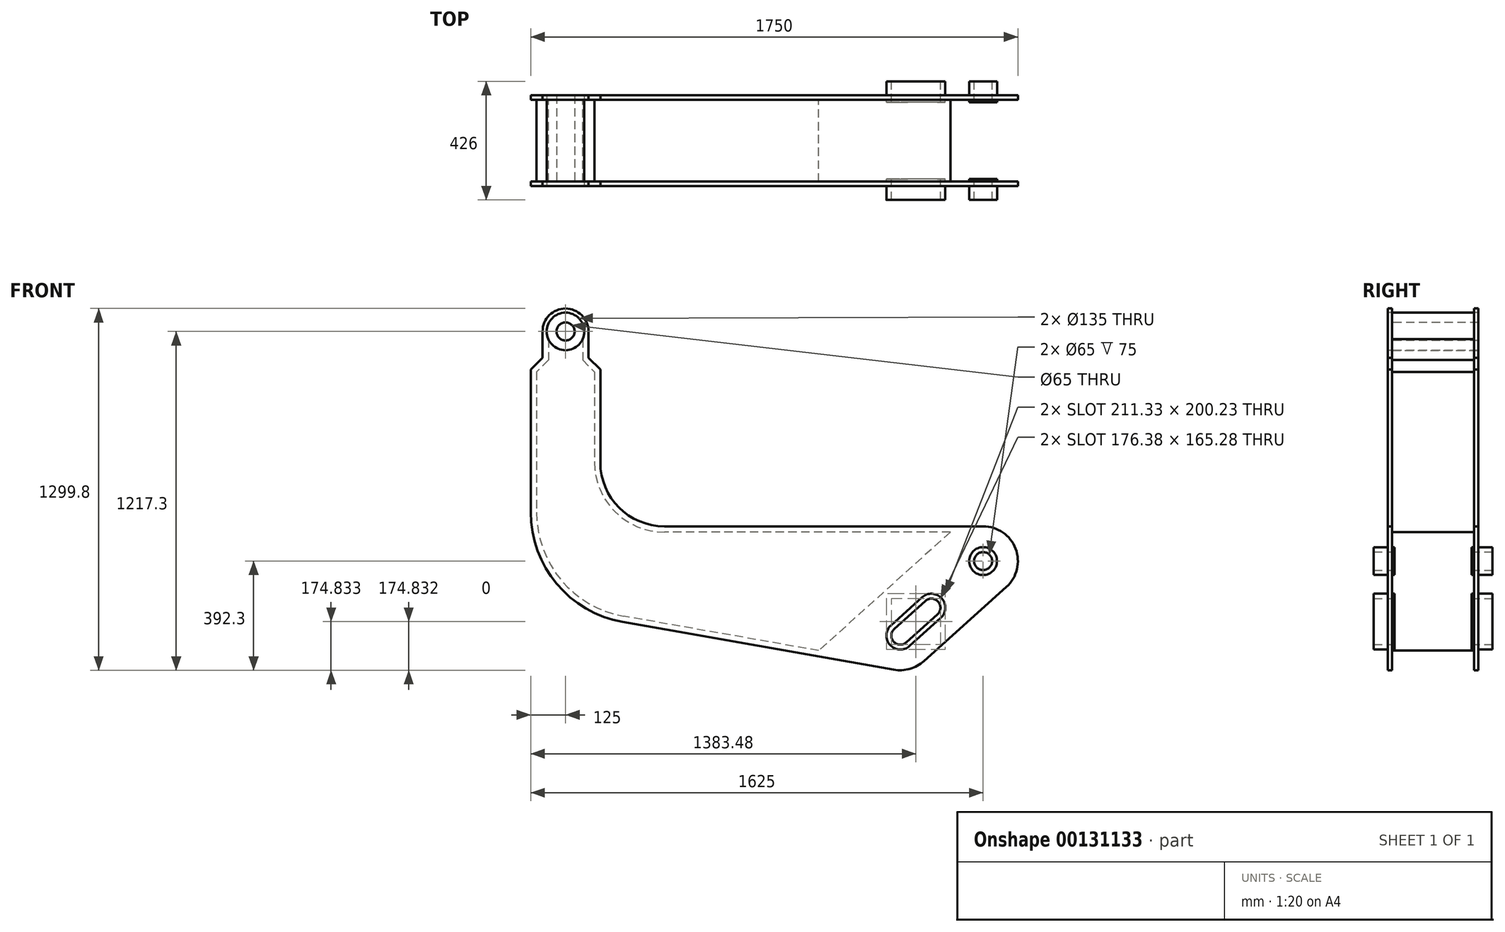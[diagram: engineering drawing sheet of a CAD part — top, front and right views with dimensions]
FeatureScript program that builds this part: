
annotation { "Feature Type Name" : "Feature", "Feature Type Description" : "" }
export const myFeature = defineFeature(function(context is Context, id is Id, definition is map)
    precondition{}
    {
        {
            var Q0;
            Q0=qCreatedBy(makeId("Front.planeOp"),FACE);
            var sketch = newSketch(context, id + "F0", { "sketchPlane" : qUnion([Q0])});
            skCircle(sketch, "E0", {"center": v(0, 0) * mm, "radius": 32.5 * mm});
            skCircle(sketch, "E1.0", {"center": v(0, 0) * mm, "radius": 82.5 * mm});
            skLineSegment(sketch, "E2", {"start": v(-82.5, 0) * mm, "end": v(-82.5, -94.13) * mm});
            skLineSegment(sketch, "E3", {"start": v(82.5, 0) * mm, "end": v(82.5, -94.13) * mm});
            skLineSegment(sketch, "E4", {"start": v(-82.5, -94.13) * mm, "end": v(-125, -136.63) * mm});
            skLineSegment(sketch, "E5", {"start": v(82.5, -94.13) * mm, "end": v(125, -136.63) * mm});
            skCircle(sketch, "E6", {"center": v(1500, -825) * mm, "radius": 32.5 * mm});
            skArc(sketch, "E7", {"start": v(1583.64, -917.9) * mm, "mid": v(1616.7, -780.2) * mm, "end": v(1500, -700) * mm});
            skCircle(sketch, "E8", {"center": v(1500, -825) * mm, "radius": 100 * mm});
            skLineSegment(sketch, "E9", {"start": v(1500, -825) * mm, "end": v(997.38, -825) * mm, "construction": true});
            skLineSegment(sketch, "E10", {"start": v(1500, -825) * mm, "end": v(1202.74, -1092.65) * mm, "construction": true});
            skLineSegment(sketch, "E11", {"start": v(1583.64, -917.9) * mm, "end": v(1288.2, -1183.91) * mm});
            skLineSegment(sketch, "E12", {"start": v(1178.63, -1215.33) * mm, "end": v(205.54, -1043.75) * mm});
            skLineSegment(sketch, "E13", {"start": v(1241.08, -1226.34) * mm, "end": v(892.28, -1226.34) * mm, "construction": true});
            skLineSegment(sketch, "E14", {"start": v(-125, -136.63) * mm, "end": v(-125, -649.82) * mm});
            skPoint(sketch, "E15.visualSharp", {"position": v(1241.08, -1226.34) * mm});
            skArc(sketch, "E15.filletArc", {"start": v(1178.63, -1215.33) * mm, "mid": v(1237.04, -1212.27) * mm, "end": v(1288.2, -1183.91) * mm});
            skPoint(sketch, "E16.visualSharp", {"position": v(-125, -985.46) * mm});
            skArc(sketch, "E16.filletArc", {"start": v(-125, -649.82) * mm, "mid": v(-31.42, -906.94) * mm, "end": v(205.54, -1043.75) * mm});
            skLineSegment(sketch, "E17", {"start": v(125, -136.63) * mm, "end": v(125, -470) * mm});
            skLineSegment(sketch, "E18", {"start": v(1500, -700) * mm, "end": v(355, -700) * mm});
            skPoint(sketch, "E19.visualSharp", {"position": v(125, -700) * mm});
            skArc(sketch, "E19.filletArc", {"start": v(125, -470) * mm, "mid": v(192.37, -632.63) * mm, "end": v(355, -700) * mm});
            skCircle(sketch, "E20", {"center": v(0, 0) * mm, "radius": 50 * mm});
            skCircle(sketch, "E21", {"center": v(1500, -825) * mm, "radius": 50 * mm});
            skCircle(sketch, "E22.0", {"center": v(0, 0) * mm, "radius": 67.5 * mm});
            skArc(sketch, "E23", {"start": v(1335.96, -1016.43) * mm, "mid": v(1338.37, -970.54) * mm, "end": v(1292.47, -968.13) * mm});
            skLineSegment(sketch, "E24", {"start": v(1335.96, -1016.43) * mm, "end": v(1224.49, -1116.8) * mm});
            skArc(sketch, "E25", {"start": v(1224.49, -1116.8) * mm, "mid": v(1178.59, -1114.4) * mm, "end": v(1181, -1068.5) * mm});
            skLineSegment(sketch, "E26", {"start": v(1292.47, -968.13) * mm, "end": v(1181, -1068.5) * mm});
            skLineSegment(sketch, "E27.0", {"start": v(1280.76, -955.13) * mm, "end": v(1169.29, -1055.5) * mm});
            skArc(sketch, "E27.1", {"start": v(1347.67, -1029.44) * mm, "mid": v(1351.37, -958.83) * mm, "end": v(1280.76, -955.13) * mm});
            skLineSegment(sketch, "E27.2", {"start": v(1347.67, -1029.44) * mm, "end": v(1236.2, -1129.8) * mm});
            skArc(sketch, "E27.3", {"start": v(1236.2, -1129.8) * mm, "mid": v(1165.58, -1126.1) * mm, "end": v(1169.29, -1055.5) * mm});
            skLineSegment(sketch, "E28.0", {"start": v(1247.3, -917.97) * mm, "end": v(1135.83, -1018.34) * mm});
            skArc(sketch, "E28.1", {"start": v(1381.13, -1066.6) * mm, "mid": v(1388.53, -925.37) * mm, "end": v(1247.3, -917.97) * mm});
            skLineSegment(sketch, "E28.2", {"start": v(1381.13, -1066.6) * mm, "end": v(1269.66, -1166.97) * mm});
            skArc(sketch, "E28.3", {"start": v(1269.66, -1166.97) * mm, "mid": v(1128.43, -1159.57) * mm, "end": v(1135.83, -1018.34) * mm});
            skSolve(sketch);
        }
        {
            var Q0;
            Q0 = qSketchRegion(id + "F0", true);
            var Q1;
            Q1=makeQuery(id+"F0.imprint","IMPRINT",FACE,{"disambiguationData":[TD([[makeQuery(id+"F0.imprint","IMPRINT",EDGE,{"derivedFrom":sQuery(id+"F0.wireOp",EDGE,"E8")}),1.0]])]});
            var Q2;
            Q2=makeQuery(id+"F0.imprint","IMPRINT",FACE,{"disambiguationData":[TD([[makeQuery(id+"F0.imprint","IMPRINT",EDGE,{"derivedFrom":sQuery(id+"F0.wireOp",EDGE,"VV7gzSqa-Ojlq-ZYf3-16EK-QqAcn2rNi812")}),1.0]])]});
            var Q3;
            Q3=makeQuery(id+"F0.imprint","IMPRINT",FACE,{"disambiguationData":[TD([[makeQuery(id+"F0.imprint","IMPRINT",EDGE,{"derivedFrom":sQuery(id+"F0.wireOp",EDGE,"E27.0")}),-1.0]])]});
            extrude(context, id + "F1", {"entities" : qUnion([Q0, Q1, Q2, Q3]), "depth" : 16 * mm});
        }
        {
            var Q0;
            Q0=makeQuery(id+"F1.opExtrude","CAP_FACE",FACE,{"disambiguationData":[OSD([sQuery(id+"F0.wireOp",EDGE,"E1.0"),sQuery(id+"F0.wireOp",EDGE,"E2"),sQuery(id+"F0.wireOp",EDGE,"E3"),sQuery(id+"F0.wireOp",EDGE,"E4"),sQuery(id+"F0.wireOp",EDGE,"E5"),sQuery(id+"F0.wireOp",EDGE,"E7"),sQuery(id+"F0.wireOp",EDGE,"E11"),sQuery(id+"F0.wireOp",EDGE,"E12"),sQuery(id+"F0.wireOp",EDGE,"E14"),sQuery(id+"F0.wireOp",EDGE,"E15.filletArc"),sQuery(id+"F0.wireOp",EDGE,"E16.filletArc"),sQuery(id+"F0.wireOp",EDGE,"E17"),sQuery(id+"F0.wireOp",EDGE,"E18"),sQuery(id+"F0.wireOp",EDGE,"E19.filletArc"),sQuery(id+"F0.wireOp",EDGE,"E21"),sQuery(id+"F0.wireOp",EDGE,"E22.0"),sQuery(id+"F0.wireOp",EDGE,"E27.0"),sQuery(id+"F0.wireOp",EDGE,"E27.1"),sQuery(id+"F0.wireOp",EDGE,"E27.2"),sQuery(id+"F0.wireOp",EDGE,"E27.3")])],"isStart":false});
            cPlane(context, id + "F2", {"entities" : qUnion([Q0]), "cplaneType" : CPlaneType.OFFSET, "offset" : 310 * mm, "width" : 150 * mm, "height" : 150 * mm});
        }
        {
            var Q0;
            Q0=qCreatedBy(id+"F2.planeOp",FACE);
            var sketch = newSketch(context, id + "F3", { "sketchPlane" : qUnion([Q0])});
            skCircle(sketch, "E29.0", {"center": v(0, 0) * mm, "radius": 32.5 * mm});
            skCircle(sketch, "E29.1", {"center": v(0, 0) * mm, "radius": 82.5 * mm});
            skLineSegment(sketch, "E29.2", {"start": v(-82.5, 0) * mm, "end": v(-82.5, -94.13) * mm});
            skLineSegment(sketch, "E29.3", {"start": v(82.5, 0) * mm, "end": v(82.5, -94.13) * mm});
            skLineSegment(sketch, "E29.4", {"start": v(-82.5, -94.13) * mm, "end": v(-125, -136.63) * mm});
            skLineSegment(sketch, "E29.5", {"start": v(82.5, -94.13) * mm, "end": v(125, -136.63) * mm});
            skCircle(sketch, "E29.6", {"center": v(1500, -825) * mm, "radius": 32.5 * mm});
            skArc(sketch, "E29.7", {"start": v(1583.64, -917.9) * mm, "mid": v(1616.7, -780.2) * mm, "end": v(1500, -700) * mm});
            skCircle(sketch, "E29.8", {"center": v(1500, -825) * mm, "radius": 100 * mm});
            skLineSegment(sketch, "E29.9", {"start": v(1500, -825) * mm, "end": v(997.38, -825) * mm});
            skLineSegment(sketch, "E29.10", {"start": v(1500, -825) * mm, "end": v(1202.74, -1092.65) * mm});
            skLineSegment(sketch, "E29.11", {"start": v(1583.64, -917.9) * mm, "end": v(1288.2, -1183.91) * mm});
            skLineSegment(sketch, "E29.12", {"start": v(1178.63, -1215.33) * mm, "end": v(205.54, -1043.75) * mm});
            skLineSegment(sketch, "E29.13", {"start": v(1241.08, -1226.34) * mm, "end": v(892.28, -1226.34) * mm});
            skLineSegment(sketch, "E29.14", {"start": v(-125, -136.63) * mm, "end": v(-125, -649.82) * mm});
            skPoint(sketch, "E29.15", {"position": v(1241.08, -1226.34) * mm});
            skArc(sketch, "E29.16", {"start": v(1178.63, -1215.33) * mm, "mid": v(1237.04, -1212.27) * mm, "end": v(1288.2, -1183.91) * mm});
            skPoint(sketch, "E29.17", {"position": v(-125, -985.46) * mm});
            skArc(sketch, "E29.18", {"start": v(-125, -649.82) * mm, "mid": v(-31.42, -906.94) * mm, "end": v(205.54, -1043.75) * mm});
            skLineSegment(sketch, "E29.19", {"start": v(125, -136.63) * mm, "end": v(125, -470) * mm});
            skLineSegment(sketch, "E29.20", {"start": v(1500, -700) * mm, "end": v(355, -700) * mm});
            skPoint(sketch, "E29.21", {"position": v(125, -700) * mm});
            skArc(sketch, "E29.22", {"start": v(125, -470) * mm, "mid": v(192.37, -632.63) * mm, "end": v(355, -700) * mm});
            skCircle(sketch, "E29.23", {"center": v(0, 0) * mm, "radius": 50 * mm});
            skCircle(sketch, "E29.24", {"center": v(1500, -825) * mm, "radius": 50 * mm});
            skCircle(sketch, "E29.25", {"center": v(0, 0) * mm, "radius": 67.5 * mm});
            skArc(sketch, "E29.26", {"start": v(1335.96, -1016.43) * mm, "mid": v(1338.37, -970.54) * mm, "end": v(1292.47, -968.13) * mm});
            skLineSegment(sketch, "E29.27", {"start": v(1335.96, -1016.43) * mm, "end": v(1224.49, -1116.8) * mm});
            skArc(sketch, "E29.28", {"start": v(1224.49, -1116.8) * mm, "mid": v(1178.59, -1114.4) * mm, "end": v(1181, -1068.5) * mm});
            skLineSegment(sketch, "E29.29", {"start": v(1292.47, -968.13) * mm, "end": v(1181, -1068.5) * mm});
            skLineSegment(sketch, "E29.30", {"start": v(1280.76, -955.13) * mm, "end": v(1169.29, -1055.5) * mm});
            skArc(sketch, "E29.31", {"start": v(1347.67, -1029.44) * mm, "mid": v(1351.37, -958.83) * mm, "end": v(1280.76, -955.13) * mm});
            skLineSegment(sketch, "E29.32", {"start": v(1347.67, -1029.44) * mm, "end": v(1236.2, -1129.8) * mm});
            skArc(sketch, "E29.33", {"start": v(1236.2, -1129.8) * mm, "mid": v(1165.58, -1126.1) * mm, "end": v(1169.29, -1055.5) * mm});
            skLineSegment(sketch, "E29.34", {"start": v(1247.3, -917.97) * mm, "end": v(1135.83, -1018.34) * mm});
            skArc(sketch, "E29.35", {"start": v(1381.13, -1066.6) * mm, "mid": v(1388.53, -925.37) * mm, "end": v(1247.3, -917.97) * mm});
            skLineSegment(sketch, "E29.36", {"start": v(1381.13, -1066.6) * mm, "end": v(1269.66, -1166.97) * mm});
            skArc(sketch, "E29.37", {"start": v(1269.66, -1166.97) * mm, "mid": v(1128.43, -1159.57) * mm, "end": v(1135.83, -1018.34) * mm});
            skSolve(sketch);
        }
        {
            var Q0;
            Q0 = qSketchRegion(id + "F3", true);
            var Q1;
            {var subQ0=sQuery(id+"F3.wireOp",EDGE,"E29.9");var subQ1=sQuery(id+"F3.wireOp",EDGE,"E29.8");var subQ2=makeQuery(id+"F3.imprint","INTERSECT",VERTEX,{"derivedFrom":[subQ1,subQ0]});Q1=makeQuery(id+"F3.imprint","IMPRINT",FACE,{"disambiguationData":[TD([[makeQuery(id+"F3.imprint","IMPRINT",EDGE,{"disambiguationData":[TD([[subQ2,1.0]])],"derivedFrom":subQ1}),1.0]])]});}
            var Q2;
            {var subQ0=sQuery(id+"F3.wireOp",EDGE,"E29.9");var subQ1=sQuery(id+"F3.wireOp",EDGE,"E29.8");var subQ2=makeQuery(id+"F3.imprint","INTERSECT",VERTEX,{"derivedFrom":[subQ1,subQ0]});Q2=makeQuery(id+"F3.imprint","IMPRINT",FACE,{"disambiguationData":[TD([[makeQuery(id+"F3.imprint","IMPRINT",EDGE,{"disambiguationData":[TD([[subQ2,-1.0]])],"derivedFrom":subQ1}),1.0]])]});}
            var Q3;
            {var subQ0=sQuery(id+"F3.wireOp",EDGE,"E29.9");var subQ1=sQuery(id+"F3.wireOp",EDGE,"E29.8");var subQ2=makeQuery(id+"F3.imprint","INTERSECT",VERTEX,{"derivedFrom":[subQ1,subQ0]});Q3=makeQuery(id+"F3.imprint","IMPRINT",FACE,{"disambiguationData":[TD([[makeQuery(id+"F3.imprint","IMPRINT",EDGE,{"disambiguationData":[TD([[subQ2,1.0]])],"derivedFrom":subQ1}),-1.0]])]});}
            var Q4;
            {var subQ0=sQuery(id+"F3.wireOp",EDGE,"E29.9");var subQ1=sQuery(id+"F3.wireOp",EDGE,"E29.8");var subQ2=makeQuery(id+"F3.imprint","INTERSECT",VERTEX,{"derivedFrom":[subQ1,subQ0]});Q4=makeQuery(id+"F3.imprint","IMPRINT",FACE,{"disambiguationData":[TD([[makeQuery(id+"F3.imprint","IMPRINT",EDGE,{"disambiguationData":[TD([[subQ2,-1.0]])],"derivedFrom":subQ1}),-1.0]])]});}
            var Q5;
            {var subQ2=sQuery(id+"F3.wireOp",EDGE,"E29.30");Q5=makeQuery(id+"F3.imprint","IMPRINT",FACE,{"disambiguationData":[TD([[makeQuery(id+"F3.imprint","IMPRINT",EDGE,{"derivedFrom":subQ2}),-1.0]])]});}
            extrude(context, id + "F4", {"entities" : qUnion([Q0, Q1, Q2, Q3, Q4, Q5]), "oppositeDirection" : true, "depth" : 16 * mm});
        }
        {
            var Q0;
            Q0=makeQuery(id+"F1.opExtrude","CAP_FACE",FACE,{"disambiguationData":[OSD([sQuery(id+"F0.wireOp",EDGE,"E0"),sQuery(id+"F0.wireOp",EDGE,"E1.0"),sQuery(id+"F0.wireOp",EDGE,"E2"),sQuery(id+"F0.wireOp",EDGE,"E3"),sQuery(id+"F0.wireOp",EDGE,"E4"),sQuery(id+"F0.wireOp",EDGE,"E5"),sQuery(id+"F0.wireOp",EDGE,"E7"),sQuery(id+"F0.wireOp",EDGE,"E11"),sQuery(id+"F0.wireOp",EDGE,"E12"),sQuery(id+"F0.wireOp",EDGE,"E14"),sQuery(id+"F0.wireOp",EDGE,"E15.filletArc"),sQuery(id+"F0.wireOp",EDGE,"E16.filletArc"),sQuery(id+"F0.wireOp",EDGE,"E17"),sQuery(id+"F0.wireOp",EDGE,"E18"),sQuery(id+"F0.wireOp",EDGE,"E19.filletArc"),sQuery(id+"F0.wireOp",EDGE,"E21"),sQuery(id+"F0.wireOp",EDGE,"NVSJcbsx-t4oL-S8TC-E93Z-FQbPMW0S7kzD")])],"isStart":false});
            var sketch = newSketch(context, id + "F5", { "sketchPlane" : qUnion([Q0])});
            skLineSegment(sketch, "E30.0", {"start": v(125, -136.63) * mm, "end": v(125, -470) * mm});
            skLineSegment(sketch, "E30.3", {"start": v(-125, -136.63) * mm, "end": v(-125, -649.82) * mm});
            skArc(sketch, "E30.4", {"start": v(125, -470) * mm, "mid": v(192.37, -632.63) * mm, "end": v(355, -700) * mm});
            skLineSegment(sketch, "E30.5", {"start": v(1500, -700) * mm, "end": v(355, -700) * mm});
            skArc(sketch, "E30.6", {"start": v(-125, -649.82) * mm, "mid": v(-31.42, -906.94) * mm, "end": v(205.54, -1043.75) * mm});
            skLineSegment(sketch, "E30.7", {"start": v(1178.63, -1215.33) * mm, "end": v(205.54, -1043.75) * mm});
            skPoint(sketch, "E30.1.start.orphan", {"position": v(82.5, -94.13) * mm});
            skPoint(sketch, "E30.2.start.orphan", {"position": v(-82.5, -94.13) * mm});
            skLineSegment(sketch, "E31.0", {"start": v(-82.5, -94.13) * mm, "end": v(-125, -136.63) * mm});
            skLineSegment(sketch, "E31.1", {"start": v(-82.5, 0) * mm, "end": v(-82.5, -94.13) * mm});
            skLineSegment(sketch, "E32.0", {"start": v(82.5, -94.13) * mm, "end": v(125, -136.63) * mm});
            skLineSegment(sketch, "E32.1", {"start": v(82.5, 0) * mm, "end": v(82.5, -94.13) * mm});
            skLineSegment(sketch, "E33.0", {"start": v(1398, -715) * mm, "end": v(355, -715) * mm});
            skLineSegment(sketch, "E33.1", {"start": v(67.5, 0) * mm, "end": v(67.5, -100.34) * mm});
            skLineSegment(sketch, "E33.2", {"start": v(67.5, -100.34) * mm, "end": v(110, -142.84) * mm});
            skLineSegment(sketch, "E33.3", {"start": v(110, -142.84) * mm, "end": v(110, -470) * mm});
            skArc(sketch, "E33.4", {"start": v(110, -470) * mm, "mid": v(181.76, -643.24) * mm, "end": v(355, -715) * mm});
            skLineSegment(sketch, "E34.0", {"start": v(911.54, -1153) * mm, "end": v(208.15, -1028.97) * mm});
            skLineSegment(sketch, "E34.1", {"start": v(-67.5, 0) * mm, "end": v(-67.5, -100.34) * mm});
            skLineSegment(sketch, "E34.2", {"start": v(-67.5, -100.34) * mm, "end": v(-110, -142.84) * mm});
            skLineSegment(sketch, "E34.3", {"start": v(-110, -142.84) * mm, "end": v(-110, -649.82) * mm});
            skArc(sketch, "E34.4", {"start": v(-110, -649.82) * mm, "mid": v(-19.93, -897.3) * mm, "end": v(208.15, -1028.97) * mm});
            skLineSegment(sketch, "E35.0", {"start": v(909.7, -1146.59) * mm, "end": v(209.19, -1023.07) * mm});
            skLineSegment(sketch, "E35.1", {"start": v(-61.5, 0) * mm, "end": v(-61.5, -102.83) * mm});
            skLineSegment(sketch, "E35.2", {"start": v(-61.5, -102.83) * mm, "end": v(-104, -145.33) * mm});
            skLineSegment(sketch, "E35.3", {"start": v(-104, -145.33) * mm, "end": v(-104, -649.82) * mm});
            skArc(sketch, "E35.4", {"start": v(-104, -649.82) * mm, "mid": v(-15.33, -893.44) * mm, "end": v(209.19, -1023.07) * mm});
            skLineSegment(sketch, "E36.0", {"start": v(1382.37, -721) * mm, "end": v(355, -721) * mm});
            skLineSegment(sketch, "E36.1", {"start": v(61.5, 0) * mm, "end": v(61.5, -102.83) * mm});
            skLineSegment(sketch, "E36.2", {"start": v(61.5, -102.83) * mm, "end": v(104, -145.33) * mm});
            skLineSegment(sketch, "E36.3", {"start": v(104, -145.33) * mm, "end": v(104, -470) * mm});
            skArc(sketch, "E36.4", {"start": v(104, -470) * mm, "mid": v(177.52, -647.48) * mm, "end": v(355, -721) * mm});
            skLineSegment(sketch, "E37.0", {"start": v(1500, -825) * mm, "end": v(1202.74, -1092.65) * mm, "construction": true});
            skLineSegment(sketch, "E38", {"start": v(1398, -715) * mm, "end": v(911.54, -1153) * mm});
            skLineSegment(sketch, "E39.0", {"start": v(1382.37, -721) * mm, "end": v(909.7, -1146.59) * mm});
            skLineSegment(sketch, "E40", {"start": v(61.5, 0) * mm, "end": v(67.5, 0) * mm});
            skLineSegment(sketch, "E41", {"start": v(-67.5, 0) * mm, "end": v(-61.5, 0) * mm});
            skSolve(sketch);
        }
        {
            var Q0;
            Q0=makeQuery(id+"F0.imprint","IMPRINT",FACE,{"disambiguationData":[TD([[makeQuery(id+"F0.imprint","IMPRINT",EDGE,{"derivedFrom":sQuery(id+"F0.wireOp",EDGE,"E6")}),-1.0]])]});
            var Q1;
            Q1=makeQuery(id+"F0.imprint","IMPRINT",FACE,{"disambiguationData":[TD([[makeQuery(id+"F0.imprint","IMPRINT",EDGE,{"derivedFrom":sQuery(id+"F0.wireOp",EDGE,"Xk7Gvi74-D533-aMbm-up9p-guu7ESpjutRq")}),-1.0]])]});
            var Q2;
            Q2=makeQuery(id+"F0.imprint","IMPRINT",FACE,{"disambiguationData":[TD([[makeQuery(id+"F0.imprint","IMPRINT",EDGE,{"derivedFrom":sQuery(id+"F0.wireOp",EDGE,"E23")}),-1.0]])]});
            extrude(context, id + "F6", {"entities" : qUnion([Q0, Q1, Q2]), "operationType" : NewBodyOperationType.ADD, "depth" : 25 * mm, "hasSecondDirection" : true, "secondDirectionOppositeDirection" : true, "secondDirectionDepth" : 50 * mm});
        }
        {
            var Q0;
            Q0=makeQuery(id+"F3.imprint","IMPRINT",FACE,{"disambiguationData":[TD([[makeQuery(id+"F3.imprint","IMPRINT",EDGE,{"derivedFrom":sQuery(id+"F3.wireOp",EDGE,"E29.23")}),1.0]])]});
            var Q1;
            Q1=makeQuery(id+"F3.imprint","IMPRINT",FACE,{"disambiguationData":[TD([[makeQuery(id+"F3.imprint","IMPRINT",EDGE,{"derivedFrom":sQuery(id+"F3.wireOp",EDGE,"E29.23")}),-1.0]])]});
            var Q2;
            Q2=qCreatedBy(makeId("Front.planeOp"),FACE);
            extrude(context, id + "F7", {"entities" : qUnion([Q0, Q1]), "endBound" : BoundingType.UP_TO_SURFACE, "oppositeDirection" : true, "endBoundEntityFace" : qUnion([Q2]), "depth" : 25 * mm});
        }
        {
            var Q0;
            Q0=makeQuery(id+"F5.imprint","IMPRINT",FACE,{"disambiguationData":[TD([[makeQuery(id+"F5.imprint","IMPRINT",EDGE,{"derivedFrom":sQuery(id+"F5.wireOp",EDGE,"E35.0")}),-1.0]])]});
            var Q1;
            Q1=makeQuery(id+"F4.opExtrude","CAP_FACE",FACE,{"disambiguationData":[OSD([sQuery(id+"F3.wireOp",EDGE,"E29.1"),sQuery(id+"F3.wireOp",EDGE,"E29.2"),sQuery(id+"F3.wireOp",EDGE,"E29.3"),sQuery(id+"F3.wireOp",EDGE,"E29.4"),sQuery(id+"F3.wireOp",EDGE,"E29.5"),sQuery(id+"F3.wireOp",EDGE,"E29.7"),sQuery(id+"F3.wireOp",EDGE,"E29.11"),sQuery(id+"F3.wireOp",EDGE,"E29.12"),sQuery(id+"F3.wireOp",EDGE,"E29.14"),sQuery(id+"F3.wireOp",EDGE,"E29.16"),sQuery(id+"F3.wireOp",EDGE,"E29.18"),sQuery(id+"F3.wireOp",EDGE,"E29.19"),sQuery(id+"F3.wireOp",EDGE,"E29.20"),sQuery(id+"F3.wireOp",EDGE,"E29.22"),sQuery(id+"F3.wireOp",EDGE,"E29.24"),sQuery(id+"F3.wireOp",EDGE,"E29.25"),sQuery(id+"F3.wireOp",EDGE,"E29.30"),sQuery(id+"F3.wireOp",EDGE,"E29.31"),sQuery(id+"F3.wireOp",EDGE,"E29.32"),sQuery(id+"F3.wireOp",EDGE,"E29.33")])],"isStart":false});
            extrude(context, id + "F8", {"entities" : qUnion([Q0]), "endBound" : BoundingType.UP_TO_SURFACE, "endBoundEntityFace" : qUnion([Q1]), "depth" : 25 * mm});
        }
        {
            var Q0;
            {var subQ0=sQuery(id+"F3.wireOp",EDGE,"E29.9");var subQ1=sQuery(id+"F3.wireOp",EDGE,"E29.6");var subQ2=makeQuery(id+"F3.imprint","INTERSECT",VERTEX,{"derivedFrom":[subQ1,subQ0]});Q0=makeQuery(id+"F3.imprint","IMPRINT",FACE,{"disambiguationData":[TD([[makeQuery(id+"F3.imprint","IMPRINT",EDGE,{"disambiguationData":[TD([[subQ2,1.0]])],"derivedFrom":subQ1}),-1.0]])]});}
            var Q1;
            {var subQ0=sQuery(id+"F3.wireOp",EDGE,"E29.9");var subQ1=sQuery(id+"F3.wireOp",EDGE,"E29.6");var subQ2=makeQuery(id+"F3.imprint","INTERSECT",VERTEX,{"derivedFrom":[subQ1,subQ0]});Q1=makeQuery(id+"F3.imprint","IMPRINT",FACE,{"disambiguationData":[TD([[makeQuery(id+"F3.imprint","IMPRINT",EDGE,{"disambiguationData":[TD([[subQ2,-1.0]])],"derivedFrom":subQ1}),-1.0]])]});}
            var Q2;
            {var subQ0=sQuery(id+"F3.wireOp",EDGE,"E29.27");Q2=makeQuery(id+"F3.imprint","IMPRINT",FACE,{"disambiguationData":[TD([[makeQuery(id+"F3.imprint","IMPRINT",EDGE,{"derivedFrom":subQ0}),1.0]])]});}
            extrude(context, id + "F9", {"entities" : qUnion([Q0, Q1, Q2]), "operationType" : NewBodyOperationType.ADD, "depth" : 50 * mm, "hasSecondDirection" : true, "secondDirectionOppositeDirection" : true, "secondDirectionDepth" : 25 * mm});
        }
    });
